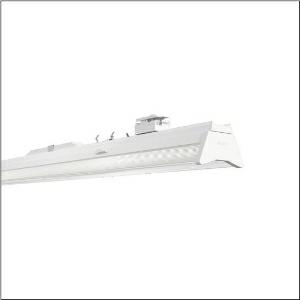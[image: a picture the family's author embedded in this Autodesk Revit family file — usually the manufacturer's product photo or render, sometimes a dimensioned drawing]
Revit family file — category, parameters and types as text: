
# Revit family: licross_21_performance_mo_52td167n485g
name_source: partatom
category: Lighting Fixtures
units: mm (PartAtom-declared; Revit-internal decimal feet)

## family parameters
Cut with Voids When Loaded = No
Host = Face
Light Source = No
Part Type = Normal
Room Calculation Point = No
Round Connector Dimension = Use Diameter
Shared = No

## types (1)
- Licross 21 Performance MO (1 x LED, 8720 lm, 47.9 W, 4000K)
    Apparent Load = 48 VA
    CIE Flux Codes = 66 88 96 79 100
    Color Rendering = 80
    Color Temperature = 4000K
    Default Elevation = 1800 mm
    Description = Licross 21 Performance MO, luminaire insert, of sheet steel, galvanised, coil coated, white, length: 1.500mm, width: 120mm, height: 123mm, LED rated luminous flux: 8.720lm, light colour: 840, SDCM (Standard Deviation of Colour Matching)MacAdam ≤ 3 SDCM (initial), control gear: ON/OFF, with plug, 3-pole, with phase selection, mains connection: 220..240V, AC, 50/60Hz, rated input power: 48W, internal wiring halogen-free, primary light control with lens, of plastic, primary optical cover: cover, of PMMA, light emission: direct/indirect distribution, primary light characteristic: symmetric, protection rating (complete): IP54, insulation class (complete): insulation class I (protective earthing), certification: CE, ENEC, UKCA, protection symbol: D if used in an environment with non-conductive dust loads with corresponding accessories, impact resistance: IK06, permissible ambient temperature for indoor applications: -35..+45°C, corresponds to IFS (International Featured Standards) requirements for safety and quality in the food industry, reducing of maximum allowable ambient temperature of 5°C with ceiling mounting, LABS conformity tested according to VDMA 24364:2018-05, The light source and the operating device comply with the requirements of the Ecodesign Regulation (EU) 2019/2020 and are replaceable in accordance with this regulation, packaging unit: 1 piece
    Height = 114 mm
    Lamp = 1 x LED
    Lamp Light Flux = 8720 lm
    Lamp Power = 47.9 W
    Lamp count = 1
    Length = 1500 mm
    Luminous efficacy = 182 lm/W
    Manufacturer = Siteco
    ModVariant = No
    Model = 52TD167N485G
    Mounting Place = Ceiling
    Mounting Type = Pendant
    Number of Poles = 1
    OnlyDefault = Yes
    Power Factor = 1
    Product Name = Licross 21 Performance MO
    Product group = luminaire insert | ceiling pendant
    ProductGroupID = 901
    Protection Class = Protection class I
    Protection Degree = IP 54
    RLX_Detail_Level = 1
    RLX_Emergency_Light_Flux = 0 lm
    RLX_Emergency_Type = 0
    RLX_Emergency_Type_DB = No
    RlxData = <blob elided: 30649 chars, md5=70b18b7f>
    Socket = socket
    Standby Power = 0 W
    System Light Flux = 8720 lm
    System Power = 48 W
    Type Comments = Product without accessories
    Type Image = l_1256138.jpg
    URL = http://relux.com
    VarID = ---
    Voltage = 0 V
    Weight = 0.00 kg
    Width = 120 mm

## geometry (parser evidence)
native form markers: Blend x4, Sweep x12
no freeform markers — native parametric forms only
